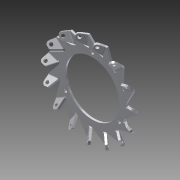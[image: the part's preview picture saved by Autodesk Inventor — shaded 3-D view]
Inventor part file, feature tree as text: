
AUTODESK INVENTOR PART (.ipt)
format: ipt  version: 2015 SP1 (Build 190203100, 203)  size: 518,656 bytes
history: native  units: in
note: dims shown in document units (in); Inventor stores cm internally (conversion verified against a paired STEP export)
features: fillet x1, other x1, imported_body x1
ambient origin geometry x8: Origin, YZ Plane, XZ Plane, XY Plane, X Axis, Y Axis, Z Axis, Center Point
bodies: Body1 (feature_tree)
feature tree (3):
  fillet  "Fillet1"  [1 undecoded]
  other  "Right Plate HD.ipt1"
  imported_body  "Base1"
note: 1 required parameter value undecoded (feature->parameter linkage not recoverable at this tier; creation-order binding heuristic only, values carry confidence <= 0.55)
